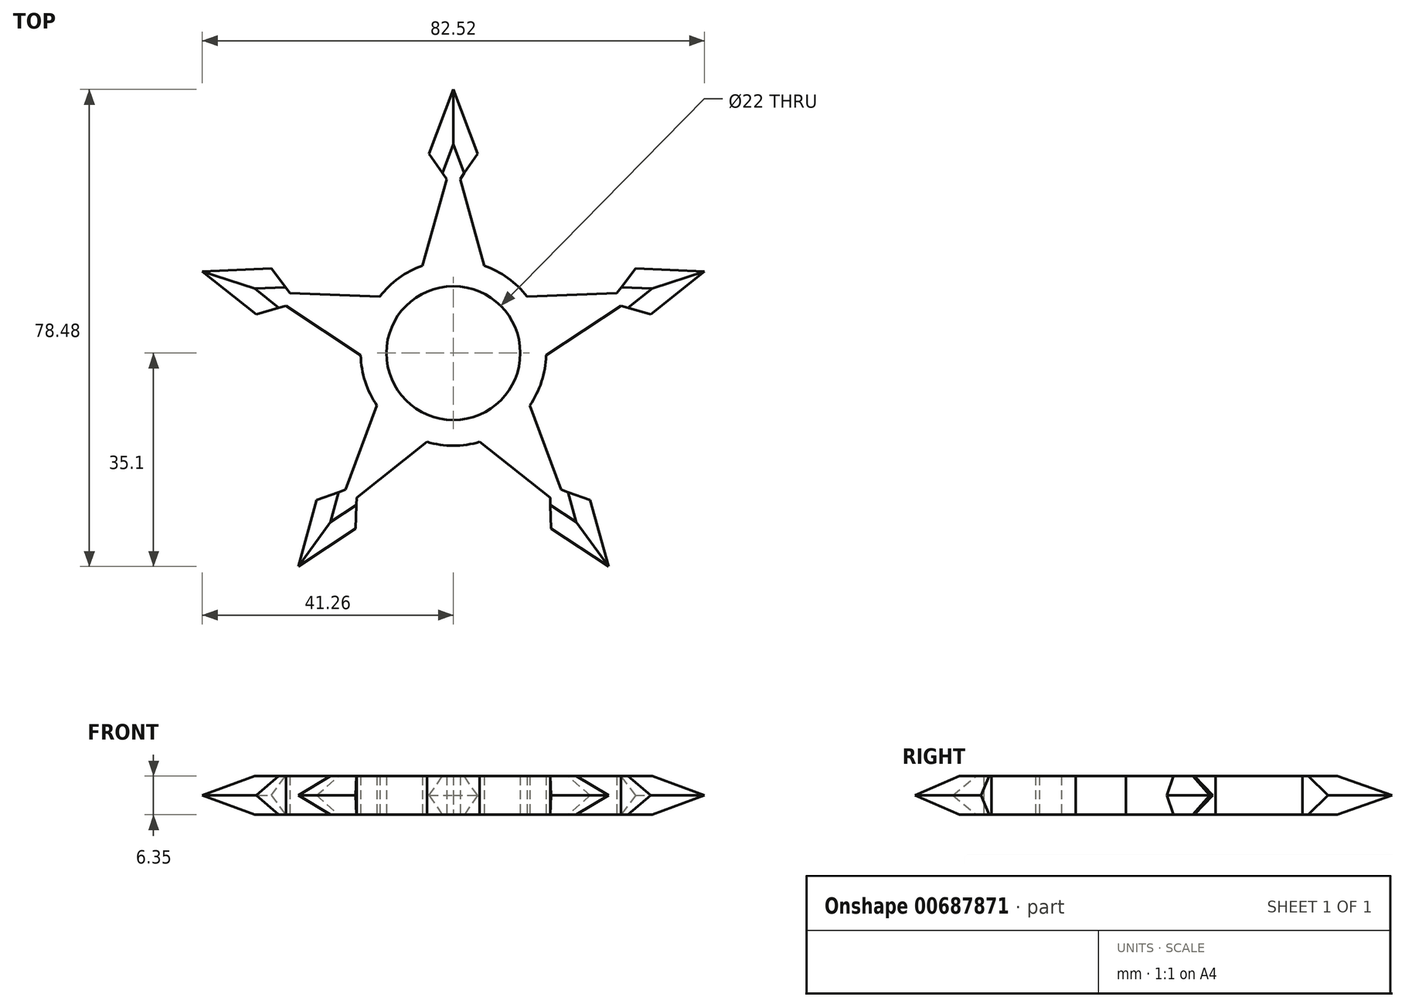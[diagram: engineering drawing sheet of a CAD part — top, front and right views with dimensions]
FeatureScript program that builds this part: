
annotation { "Feature Type Name" : "Feature", "Feature Type Description" : "" }
export const myFeature = defineFeature(function(context is Context, id is Id, definition is map)
    precondition{}
    {
        {
            var Q0;
            Q0=qCreatedBy(makeId("Top.planeOp"),FACE);
            var sketch = newSketch(context, id + "F0", { "sketchPlane" : qUnion([Q0])});
            skCircle(sketch, "E0", {"center": v(0, 0) * mm, "radius": 11 * mm});
            skLineSegment(sketch, "E1", {"start": v(-5.08, 14.37) * mm, "end": v(-1.11, 28.6) * mm});
            skLineSegment(sketch, "E2", {"start": v(-1.11, 28.6) * mm, "end": v(-3.98, 32.78) * mm});
            skLineSegment(sketch, "E3", {"start": v(-3.98, 32.78) * mm, "end": v(0, 43.38) * mm});
            skLineSegment(sketch, "E4.MirrorCS", {"start": v(5.08, 14.37) * mm, "end": v(1.11, 28.6) * mm});
            skLineSegment(sketch, "E5.MirrorCS", {"start": v(1.11, 28.6) * mm, "end": v(3.98, 32.78) * mm});
            skLineSegment(sketch, "E6.MirrorCS", {"start": v(3.98, 32.78) * mm, "end": v(0, 43.38) * mm});
            skLineSegment(sketch, "E7.1.0", {"start": v(-12.1, 9.27) * mm, "end": v(-26.85, 9.9) * mm});
            skLineSegment(sketch, "E7.1.1", {"start": v(-15.23, -0.4) * mm, "end": v(-27.54, 7.78) * mm});
            skLineSegment(sketch, "E7.1.2", {"start": v(-26.85, 9.9) * mm, "end": v(-29.95, 13.92) * mm});
            skLineSegment(sketch, "E7.1.3", {"start": v(-27.54, 7.78) * mm, "end": v(-32.4, 6.34) * mm});
            skLineSegment(sketch, "E7.1.4", {"start": v(-32.4, 6.34) * mm, "end": v(-41.26, 13.4) * mm});
            skLineSegment(sketch, "E7.1.5", {"start": v(-29.95, 13.92) * mm, "end": v(-41.26, 13.4) * mm});
            skLineSegment(sketch, "E7.2.0", {"start": v(-12.56, -8.64) * mm, "end": v(-17.7, -22.48) * mm});
            skLineSegment(sketch, "E7.2.1", {"start": v(-4.34, -14.61) * mm, "end": v(-15.9, -23.78) * mm});
            skLineSegment(sketch, "E7.2.2", {"start": v(-17.7, -22.48) * mm, "end": v(-22.5, -24.18) * mm});
            skLineSegment(sketch, "E7.2.3", {"start": v(-15.9, -23.78) * mm, "end": v(-16.05, -28.86) * mm});
            skLineSegment(sketch, "E7.2.4", {"start": v(-16.05, -28.86) * mm, "end": v(-25.5, -35.1) * mm});
            skLineSegment(sketch, "E7.2.5", {"start": v(-22.5, -24.18) * mm, "end": v(-25.5, -35.1) * mm});
            skLineSegment(sketch, "E7.3.0", {"start": v(4.34, -14.61) * mm, "end": v(15.9, -23.78) * mm});
            skLineSegment(sketch, "E7.3.1", {"start": v(12.56, -8.64) * mm, "end": v(17.7, -22.48) * mm});
            skLineSegment(sketch, "E7.3.2", {"start": v(15.9, -23.78) * mm, "end": v(16.05, -28.86) * mm});
            skLineSegment(sketch, "E7.3.3", {"start": v(17.7, -22.48) * mm, "end": v(22.5, -24.18) * mm});
            skLineSegment(sketch, "E7.3.4", {"start": v(22.5, -24.18) * mm, "end": v(25.5, -35.1) * mm});
            skLineSegment(sketch, "E7.3.5", {"start": v(16.05, -28.86) * mm, "end": v(25.5, -35.1) * mm});
            skLineSegment(sketch, "E7.4.0", {"start": v(15.23, -0.4) * mm, "end": v(27.54, 7.78) * mm});
            skLineSegment(sketch, "E7.4.1", {"start": v(12.1, 9.27) * mm, "end": v(26.85, 9.9) * mm});
            skLineSegment(sketch, "E7.4.2", {"start": v(27.54, 7.78) * mm, "end": v(32.4, 6.34) * mm});
            skLineSegment(sketch, "E7.4.3", {"start": v(26.85, 9.9) * mm, "end": v(29.95, 13.92) * mm});
            skLineSegment(sketch, "E7.4.4", {"start": v(29.95, 13.92) * mm, "end": v(41.26, 13.4) * mm});
            skLineSegment(sketch, "E7.4.5", {"start": v(32.4, 6.34) * mm, "end": v(41.26, 13.4) * mm});
            skArc(sketch, "E8", {"start": v(-15.23, -0.4) * mm, "mid": v(-14.5, -4.7) * mm, "end": v(-12.56, -8.64) * mm});
            skArc(sketch, "E9.trimOffspring", {"start": v(-4.34, -14.61) * mm, "mid": v(0, -15.24) * mm, "end": v(4.34, -14.61) * mm});
            skArc(sketch, "E10.trimOffspring", {"start": v(12.56, -8.64) * mm, "mid": v(14.5, -4.7) * mm, "end": v(15.23, -0.4) * mm});
            skArc(sketch, "E11.trimOffspring", {"start": v(12.1, 9.27) * mm, "mid": v(8.96, 12.33) * mm, "end": v(5.08, 14.37) * mm});
            skArc(sketch, "E12.trimOffspring", {"start": v(-5.08, 14.37) * mm, "mid": v(-8.96, 12.33) * mm, "end": v(-12.1, 9.27) * mm});
            skSolve(sketch);
        }
        {
            var Q0;
            Q0=makeQuery(id+"F0.imprint","IMPRINT",FACE,{"disambiguationData":[TD([[makeQuery(id+"F0.imprint","IMPRINT",EDGE,{"derivedFrom":sQuery(id+"F0.wireOp",EDGE,"E0")}),-1.0]])]});
            extrude(context, id + "F1", {"entities" : qUnion([Q0]), "depth" : 6.35 * mm, "offsetDistance" : 25.4 * mm});
        }
        {
            var Q0;
            Q0=makeQuery(id+"F1.opExtrude","CAP_EDGE",EDGE,{"disambiguationData":[OSD([sQuery(id+"F0.wireOp",EDGE,"E7.4.4")])],"isStart":false});
            var Q1;
            Q1=makeQuery(id+"F1.opExtrude","CAP_EDGE",EDGE,{"disambiguationData":[OSD([sQuery(id+"F0.wireOp",EDGE,"E7.4.4")])],"isStart":true});
            var Q2;
            Q2=makeQuery(id+"F1.opExtrude","CAP_EDGE",EDGE,{"disambiguationData":[OSD([sQuery(id+"F0.wireOp",EDGE,"E7.4.5")])],"isStart":false});
            var Q3;
            Q3=makeQuery(id+"F1.opExtrude","CAP_EDGE",EDGE,{"disambiguationData":[OSD([sQuery(id+"F0.wireOp",EDGE,"E7.4.5")])],"isStart":true});
            var Q4;
            Q4=makeQuery(id+"F1.opExtrude","CAP_EDGE",EDGE,{"disambiguationData":[OSD([sQuery(id+"F0.wireOp",EDGE,"E6.MirrorCS")])],"isStart":false});
            var Q5;
            Q5=makeQuery(id+"F1.opExtrude","CAP_EDGE",EDGE,{"disambiguationData":[OSD([sQuery(id+"F0.wireOp",EDGE,"E6.MirrorCS")])],"isStart":true});
            var Q6;
            Q6=makeQuery(id+"F1.opExtrude","CAP_EDGE",EDGE,{"disambiguationData":[OSD([sQuery(id+"F0.wireOp",EDGE,"E7.3.4")])],"isStart":false});
            var Q7;
            Q7=makeQuery(id+"F1.opExtrude","CAP_EDGE",EDGE,{"disambiguationData":[OSD([sQuery(id+"F0.wireOp",EDGE,"E7.3.4")])],"isStart":true});
            var Q8;
            Q8=makeQuery(id+"F1.opExtrude","CAP_EDGE",EDGE,{"disambiguationData":[OSD([sQuery(id+"F0.wireOp",EDGE,"E7.1.5")])],"isStart":false});
            var Q9;
            Q9=makeQuery(id+"F1.opExtrude","CAP_EDGE",EDGE,{"disambiguationData":[OSD([sQuery(id+"F0.wireOp",EDGE,"E7.1.5")])],"isStart":true});
            var Q10;
            Q10=makeQuery(id+"F1.opExtrude","CAP_EDGE",EDGE,{"disambiguationData":[OSD([sQuery(id+"F0.wireOp",EDGE,"E3")])],"isStart":false});
            var Q11;
            Q11=makeQuery(id+"F1.opExtrude","CAP_EDGE",EDGE,{"disambiguationData":[OSD([sQuery(id+"F0.wireOp",EDGE,"E3")])],"isStart":true});
            var Q12;
            Q12=makeQuery(id+"F1.opExtrude","CAP_EDGE",EDGE,{"disambiguationData":[OSD([sQuery(id+"F0.wireOp",EDGE,"E7.2.5")])],"isStart":false});
            var Q13;
            Q13=makeQuery(id+"F1.opExtrude","CAP_EDGE",EDGE,{"disambiguationData":[OSD([sQuery(id+"F0.wireOp",EDGE,"E7.2.5")])],"isStart":true});
            var Q14;
            Q14=makeQuery(id+"F1.opExtrude","CAP_EDGE",EDGE,{"disambiguationData":[OSD([sQuery(id+"F0.wireOp",EDGE,"E7.1.4")])],"isStart":false});
            var Q15;
            Q15=makeQuery(id+"F1.opExtrude","CAP_EDGE",EDGE,{"disambiguationData":[OSD([sQuery(id+"F0.wireOp",EDGE,"E7.1.4")])],"isStart":true});
            var Q16;
            Q16=makeQuery(id+"F1.opExtrude","CAP_EDGE",EDGE,{"disambiguationData":[OSD([sQuery(id+"F0.wireOp",EDGE,"E7.2.4")])],"isStart":false});
            var Q17;
            Q17=makeQuery(id+"F1.opExtrude","CAP_EDGE",EDGE,{"disambiguationData":[OSD([sQuery(id+"F0.wireOp",EDGE,"E7.2.4")])],"isStart":true});
            var Q18;
            Q18=makeQuery(id+"F1.opExtrude","CAP_EDGE",EDGE,{"disambiguationData":[OSD([sQuery(id+"F0.wireOp",EDGE,"E7.3.5")])],"isStart":false});
            var Q19;
            Q19=makeQuery(id+"F1.opExtrude","CAP_EDGE",EDGE,{"disambiguationData":[OSD([sQuery(id+"F0.wireOp",EDGE,"E7.3.5")])],"isStart":true});
            chamfer(context, id + "F2", {"entities" : qUnion([Q0, Q1, Q2, Q3, Q4, Q5, Q6, Q7, Q8, Q9, Q10, Q11, Q12, Q13, Q14, Q15, Q16, Q17, Q18, Q19]), "width" : 3.17 * mm, "tangentPropagation" : true});
        }
    });
